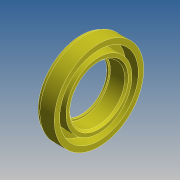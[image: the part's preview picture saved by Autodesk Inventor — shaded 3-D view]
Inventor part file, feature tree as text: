
AUTODESK INVENTOR PART (.ipt)
format: ipt  version: 2019 (Build 230136000, 136)  size: 246,272 bytes
history: native  units: mm
features: revolve x1, chamfer x1, sketch x1
ambient origin geometry x8: Origin, YZ Plane, XZ Plane, XY Plane, X Axis, Y Axis, Z Axis, Center Point
bodies: Solid1 (feature_tree)
feature tree (3):
  revolve  "Revolution1"  [1 undecoded]
  chamfer  "Chamfer1"  Distance=10.0mm
  sketch  "Sketch1"  dims[d0=49.8mm d1=47.8mm d2=10.0mm d3=1.0mm d4=2.0mm d5=30.7mm d6=1.0mm d7=3.0mm d8=3.0mm d9=3.0mm d10=10.0mm d11=90.0deg d12=1.0mm d13=2.0mm d14=45.0deg]
note: 1 required parameter value undecoded (feature->parameter linkage not recoverable at this tier; creation-order binding heuristic only, values carry confidence <= 0.55)
